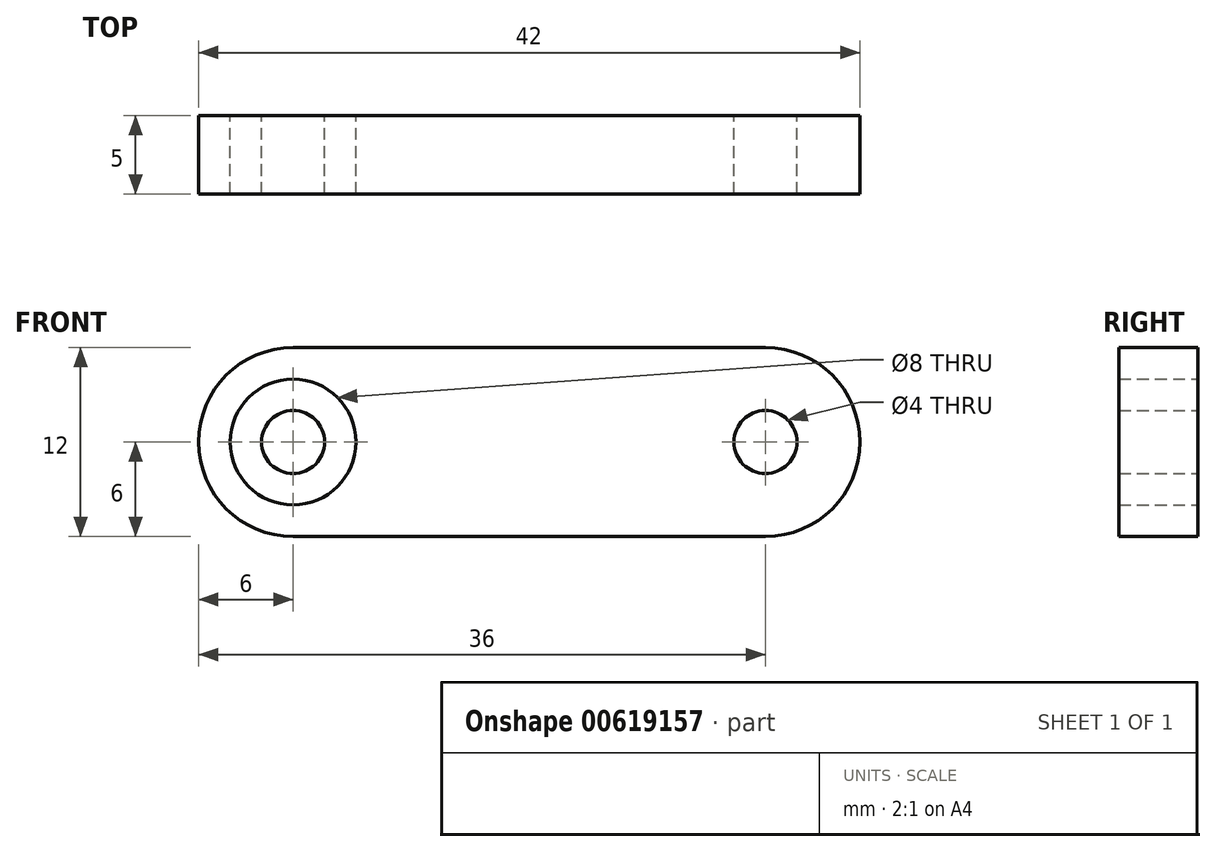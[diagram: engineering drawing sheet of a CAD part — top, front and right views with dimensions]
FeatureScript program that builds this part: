
annotation { "Feature Type Name" : "Feature", "Feature Type Description" : "" }
export const myFeature = defineFeature(function(context is Context, id is Id, definition is map)
    precondition{}
    {
        {
            var Q0;
            Q0=qCreatedBy(makeId("Front.planeOp"),FACE);
            var sketch = newSketch(context, id + "F0", { "sketchPlane" : qUnion([Q0])});
            skCircle(sketch, "E0", {"center": v(-15, 0) * mm, "radius": 2 * mm});
            skCircle(sketch, "E1", {"center": v(-15, 0) * mm, "radius": 4 * mm});
            skArc(sketch, "E2", {"start": v(-15, 6) * mm, "mid": v(-21, 0) * mm, "end": v(-15, -6) * mm});
            skLineSegment(sketch, "E3", {"start": v(0, 6) * mm, "end": v(0, 0) * mm, "construction": true});
            skLineSegment(sketch, "E4", {"start": v(-15, 6) * mm, "end": v(0, 6) * mm});
            skLineSegment(sketch, "E5", {"start": v(-15, -6) * mm, "end": v(0, -6) * mm});
            skArc(sketch, "E6.MirrorCS", {"start": v(15, 6) * mm, "mid": v(21, 0) * mm, "end": v(15, -6) * mm});
            skCircle(sketch, "E7.MirrorC", {"center": v(15, 0) * mm, "radius": 4 * mm});
            skLineSegment(sketch, "E8.MirrorCS", {"start": v(15, 6) * mm, "end": v(0, 6) * mm});
            skLineSegment(sketch, "E9.MirrorCS", {"start": v(15, -6) * mm, "end": v(0, -6) * mm});
            skCircle(sketch, "E10.MirrorC", {"center": v(15, 0) * mm, "radius": 2 * mm});
            skSolve(sketch);
        }
        {
            var Q0;
            Q0=makeQuery(id+"F0.imprint","IMPRINT",FACE,{"disambiguationData":[TD([[makeQuery(id+"F0.imprint","IMPRINT",EDGE,{"derivedFrom":sQuery(id+"F0.wireOp",EDGE,"E1")}),-1.0]])]});
            var Q1;
            Q1=makeQuery(id+"F0.imprint","IMPRINT",FACE,{"disambiguationData":[TD([[makeQuery(id+"F0.imprint","IMPRINT",EDGE,{"derivedFrom":sQuery(id+"F0.wireOp",EDGE,"E0")}),1.0]])]});
            var Q2;
            Q2=makeQuery(id+"F0.imprint","IMPRINT",FACE,{"disambiguationData":[TD([[makeQuery(id+"F0.imprint","IMPRINT",EDGE,{"derivedFrom":sQuery(id+"F0.wireOp",EDGE,"E10.MirrorC")}),-1.0]])]});
            extrude(context, id + "F1", {"entities" : qUnion([Q0, Q1, Q2]), "depth" : 5 * mm, "offsetDistance" : 25 * mm});
        }
    });
